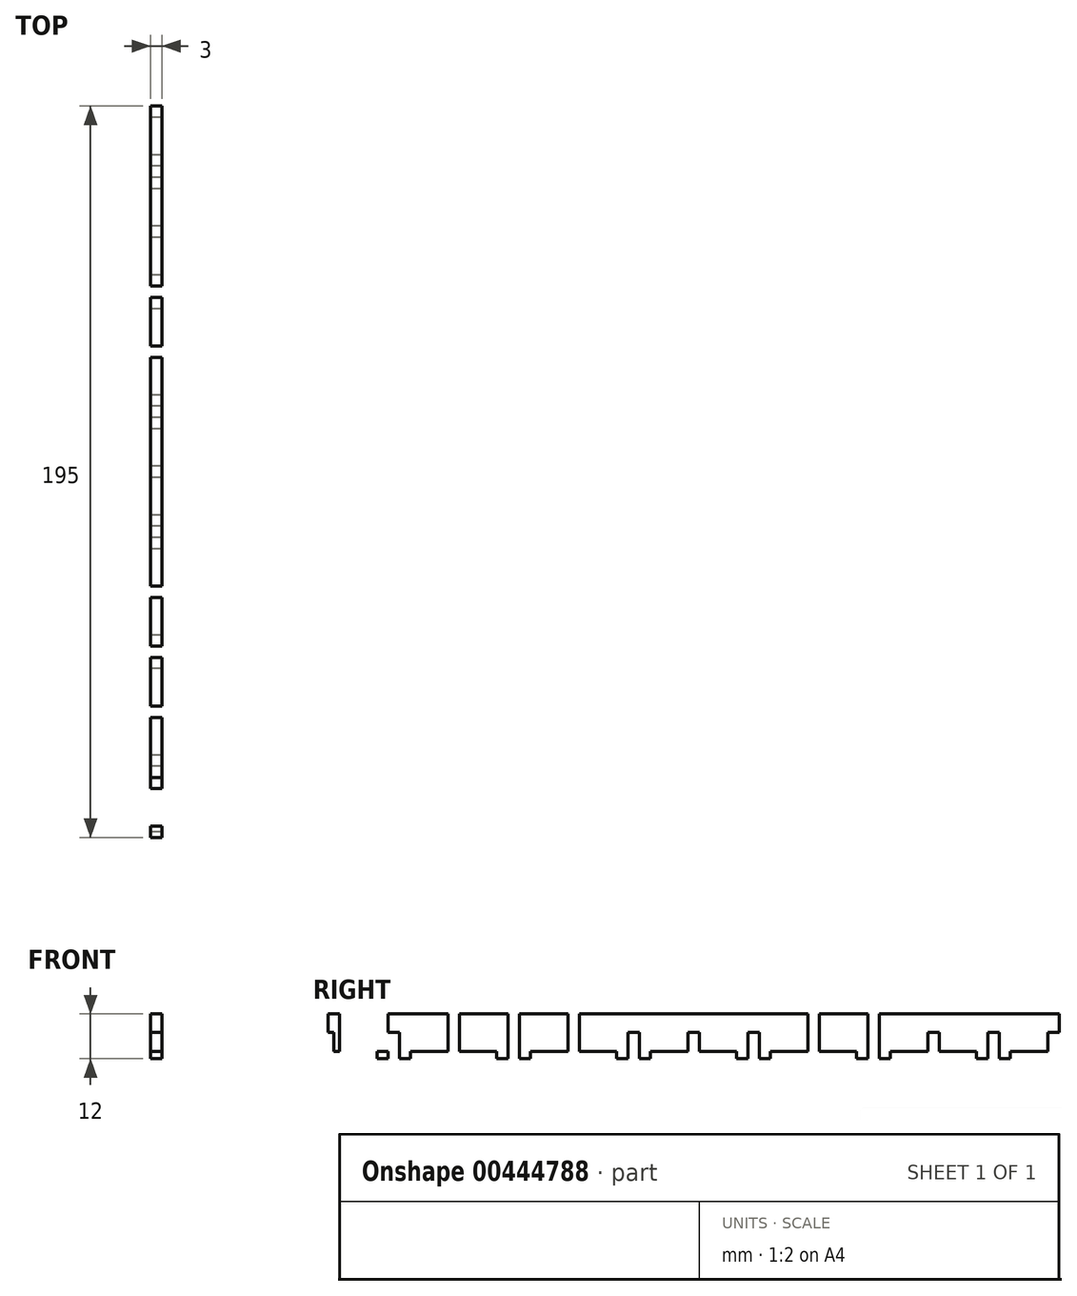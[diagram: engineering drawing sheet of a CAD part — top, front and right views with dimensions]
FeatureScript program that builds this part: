
annotation { "Feature Type Name" : "Feature", "Feature Type Description" : "" }
export const myFeature = defineFeature(function(context is Context, id is Id, definition is map)
    precondition{}
    {
        {
            var Q0;
            Q0=qCreatedBy(makeId("Right.planeOp"),FACE);
            var sketch = newSketch(context, id + "F0", { "sketchPlane" : qUnion([Q0])});
            skLineSegment(sketch, "E0", {"start": v(0, 0) * mm, "end": v(11.5, 0) * mm});
            skLineSegment(sketch, "E1", {"start": v(11.5, 0) * mm, "end": v(11.5, -2) * mm});
            skLineSegment(sketch, "E2", {"start": v(11.5, -2) * mm, "end": v(20.5, -2) * mm});
            skLineSegment(sketch, "E3", {"start": v(20.5, -2) * mm, "end": v(20.5, 0) * mm});
            skLineSegment(sketch, "E4", {"start": v(20.5, 0) * mm, "end": v(43.5, 0) * mm});
            skLineSegment(sketch, "E5", {"start": v(43.5, 0) * mm, "end": v(43.5, -2) * mm});
            skLineSegment(sketch, "E6", {"start": v(43.5, -2) * mm, "end": v(52.5, -2) * mm});
            skLineSegment(sketch, "E7", {"start": v(52.5, -2) * mm, "end": v(52.5, 0) * mm});
            skLineSegment(sketch, "E8", {"start": v(0, 0) * mm, "end": v(0, 10) * mm});
            skPoint(sketch, "E9.oppositeSnap0", {"position": v(0, 5) * mm});
            skLineSegment(sketch, "E9.bottom", {"start": v(0, 10) * mm, "end": v(-1.5, 10) * mm});
            skLineSegment(sketch, "E9.top", {"start": v(0, 5) * mm, "end": v(-1.5, 5) * mm});
            skLineSegment(sketch, "E9.left", {"start": v(0, 10) * mm, "end": v(0, 5) * mm});
            skLineSegment(sketch, "E9.right", {"start": v(-1.5, 10) * mm, "end": v(-1.5, 5) * mm});
            skLineSegment(sketch, "E10.bottom", {"start": v(14.5, 10) * mm, "end": v(17.5, 10) * mm});
            skLineSegment(sketch, "E10.top", {"start": v(14.5, 5) * mm, "end": v(17.5, 5) * mm});
            skLineSegment(sketch, "E10.left", {"start": v(14.5, 10) * mm, "end": v(14.5, 5) * mm});
            skLineSegment(sketch, "E10.right", {"start": v(17.5, 10) * mm, "end": v(17.5, 5) * mm});
            skLineSegment(sketch, "E11.top", {"start": v(0, 0) * mm, "end": v(-1.5, 0) * mm});
            skLineSegment(sketch, "E11.left", {"start": v(0, 5) * mm, "end": v(0, 0) * mm});
            skLineSegment(sketch, "E11.right", {"start": v(-1.5, 5) * mm, "end": v(-1.5, 0) * mm});
            skLineSegment(sketch, "E12.top", {"start": v(14.5, -2) * mm, "end": v(17.5, -2) * mm});
            skLineSegment(sketch, "E12.left", {"start": v(14.5, 5) * mm, "end": v(14.5, -2) * mm});
            skLineSegment(sketch, "E12.right", {"start": v(17.5, 5) * mm, "end": v(17.5, -2) * mm});
            skLineSegment(sketch, "E13.bottom", {"start": v(0, 10) * mm, "end": v(1.5, 10) * mm});
            skLineSegment(sketch, "E13.top", {"start": v(0, 5) * mm, "end": v(1.5, 5) * mm});
            skLineSegment(sketch, "E13.right", {"start": v(1.5, 10) * mm, "end": v(1.5, 5) * mm});
            skLineSegment(sketch, "E14.top", {"start": v(0, 0) * mm, "end": v(1.5, 0) * mm});
            skLineSegment(sketch, "E14.right", {"start": v(1.5, 5) * mm, "end": v(1.5, 0) * mm});
            skLineSegment(sketch, "E15.bottom", {"start": v(11.5, 10) * mm, "end": v(20.5, 10) * mm});
            skLineSegment(sketch, "E15.top", {"start": v(11.5, 13) * mm, "end": v(20.5, 13) * mm});
            skLineSegment(sketch, "E15.left", {"start": v(11.5, 10) * mm, "end": v(11.5, 13) * mm});
            skLineSegment(sketch, "E15.right", {"start": v(20.5, 10) * mm, "end": v(20.5, 13) * mm});
            skLineSegment(sketch, "E16", {"start": v(52.5, 0) * mm, "end": v(75.5, 0) * mm});
            skLineSegment(sketch, "E17", {"start": v(75.5, 0) * mm, "end": v(75.5, -2) * mm});
            skLineSegment(sketch, "E18", {"start": v(75.5, -2) * mm, "end": v(84.5, -2) * mm});
            skLineSegment(sketch, "E19", {"start": v(84.5, -2) * mm, "end": v(84.5, 0) * mm});
            skLineSegment(sketch, "E20", {"start": v(84.5, 0) * mm, "end": v(96, 0) * mm});
            skLineSegment(sketch, "E21", {"start": v(96, 0) * mm, "end": v(96, 19.13) * mm, "construction": true});
            skLineSegment(sketch, "E22", {"start": v(16, 10) * mm, "end": v(16, 11.65) * mm, "construction": true});
            skLineSegment(sketch, "E23.bottom", {"start": v(30.5, 0) * mm, "end": v(33.5, 0) * mm});
            skLineSegment(sketch, "E23.top", {"start": v(30.5, 5) * mm, "end": v(33.5, 5) * mm});
            skLineSegment(sketch, "E23.left", {"start": v(30.5, 0) * mm, "end": v(30.5, 5) * mm});
            skLineSegment(sketch, "E23.right", {"start": v(33.5, 0) * mm, "end": v(33.5, 5) * mm});
            skLineSegment(sketch, "E24.bottom", {"start": v(33.5, 5) * mm, "end": v(30.5, 5) * mm});
            skLineSegment(sketch, "E24.top", {"start": v(33.5, 10) * mm, "end": v(30.5, 10) * mm});
            skLineSegment(sketch, "E24.left", {"start": v(33.5, 5) * mm, "end": v(33.5, 10) * mm});
            skLineSegment(sketch, "E24.right", {"start": v(30.5, 5) * mm, "end": v(30.5, 10) * mm});
            skLineSegment(sketch, "E25", {"start": v(32, 0) * mm, "end": v(32, 2.31) * mm, "construction": true});
            skLineSegment(sketch, "E26.bottom", {"start": v(46.5, -2) * mm, "end": v(49.5, -2) * mm});
            skLineSegment(sketch, "E26.top", {"start": v(46.5, 5) * mm, "end": v(49.5, 5) * mm});
            skLineSegment(sketch, "E26.left", {"start": v(46.5, -2) * mm, "end": v(46.5, 5) * mm});
            skLineSegment(sketch, "E26.right", {"start": v(49.5, -2) * mm, "end": v(49.5, 5) * mm});
            skLineSegment(sketch, "E27.bottom", {"start": v(49.5, 5) * mm, "end": v(46.5, 5) * mm});
            skLineSegment(sketch, "E27.top", {"start": v(49.5, 10) * mm, "end": v(46.5, 10) * mm});
            skLineSegment(sketch, "E27.left", {"start": v(49.5, 5) * mm, "end": v(49.5, 10) * mm});
            skLineSegment(sketch, "E27.right", {"start": v(46.5, 5) * mm, "end": v(46.5, 10) * mm});
            skLineSegment(sketch, "E28.bottom", {"start": v(62.5, 0) * mm, "end": v(65.5, 0) * mm});
            skLineSegment(sketch, "E28.top", {"start": v(62.5, 5) * mm, "end": v(65.5, 5) * mm});
            skLineSegment(sketch, "E28.left", {"start": v(62.5, 0) * mm, "end": v(62.5, 5) * mm});
            skLineSegment(sketch, "E28.right", {"start": v(65.5, 0) * mm, "end": v(65.5, 5) * mm});
            skLineSegment(sketch, "E29.bottom", {"start": v(65.5, 5) * mm, "end": v(62.5, 5) * mm});
            skLineSegment(sketch, "E29.top", {"start": v(65.5, 10) * mm, "end": v(62.5, 10) * mm});
            skLineSegment(sketch, "E29.left", {"start": v(65.5, 5) * mm, "end": v(65.5, 10) * mm});
            skLineSegment(sketch, "E29.right", {"start": v(62.5, 5) * mm, "end": v(62.5, 10) * mm});
            skLineSegment(sketch, "E30.bottom", {"start": v(81.5, -2) * mm, "end": v(78.5, -2) * mm});
            skLineSegment(sketch, "E30.top", {"start": v(81.5, 5) * mm, "end": v(78.5, 5) * mm});
            skLineSegment(sketch, "E30.left", {"start": v(81.5, -2) * mm, "end": v(81.5, 5) * mm});
            skLineSegment(sketch, "E30.right", {"start": v(78.5, -2) * mm, "end": v(78.5, 5) * mm});
            skLineSegment(sketch, "E31.top", {"start": v(81.5, 10) * mm, "end": v(78.5, 10) * mm});
            skLineSegment(sketch, "E31.left", {"start": v(81.5, 5) * mm, "end": v(81.5, 10) * mm});
            skLineSegment(sketch, "E31.right", {"start": v(78.5, 5) * mm, "end": v(78.5, 10) * mm});
            skLineSegment(sketch, "E32.bottom", {"start": v(96, 0) * mm, "end": v(94.5, 0) * mm});
            skLineSegment(sketch, "E32.top", {"start": v(96, 5) * mm, "end": v(94.5, 5) * mm});
            skLineSegment(sketch, "E32.left", {"start": v(96, 0) * mm, "end": v(96, 5) * mm});
            skLineSegment(sketch, "E32.right", {"start": v(94.5, 0) * mm, "end": v(94.5, 5) * mm});
            skLineSegment(sketch, "E33.left", {"start": v(96, 5) * mm, "end": v(96, 5) * mm});
            skLineSegment(sketch, "E33.right", {"start": v(94.5, 5) * mm, "end": v(94.5, 5) * mm});
            skLineSegment(sketch, "E34.top", {"start": v(96, 10) * mm, "end": v(94.5, 10) * mm});
            skLineSegment(sketch, "E34.left", {"start": v(96, 5) * mm, "end": v(96, 10) * mm});
            skLineSegment(sketch, "E34.right", {"start": v(94.5, 5) * mm, "end": v(94.5, 10) * mm});
            skLineSegment(sketch, "E35", {"start": v(48, -2) * mm, "end": v(48, 0) * mm, "construction": true});
            skLineSegment(sketch, "E36", {"start": v(64, 0) * mm, "end": v(64, 2.67) * mm, "construction": true});
            skLineSegment(sketch, "E37", {"start": v(80, -2) * mm, "end": v(80, 0) * mm, "construction": true});
            skLineSegment(sketch, "E38", {"start": v(1.5, 10) * mm, "end": v(96, 10) * mm});
            skLineSegment(sketch, "E39.MirrorCS", {"start": v(96, 5) * mm, "end": v(97.5, 5) * mm});
            skLineSegment(sketch, "E40.MirrorCS", {"start": v(145.5, 5) * mm, "end": v(142.5, 5) * mm});
            skLineSegment(sketch, "E41.MirrorCS", {"start": v(110.5, 5) * mm, "end": v(113.5, 5) * mm});
            skLineSegment(sketch, "E42.MirrorCS", {"start": v(129.5, 5) * mm, "end": v(126.5, 5) * mm});
            skLineSegment(sketch, "E43.MirrorCS", {"start": v(177.5, 5) * mm, "end": v(174.5, 5) * mm});
            skLineSegment(sketch, "E44.MirrorCS", {"start": v(192, 5) * mm, "end": v(190.5, 5) * mm});
            skLineSegment(sketch, "E45.MirrorCS", {"start": v(192, 5) * mm, "end": v(193.5, 5) * mm});
            skLineSegment(sketch, "E46.MirrorCS", {"start": v(142.5, 5) * mm, "end": v(145.5, 5) * mm});
            skLineSegment(sketch, "E47.MirrorCS", {"start": v(126.5, 5) * mm, "end": v(129.5, 5) * mm});
            skLineSegment(sketch, "E48.MirrorCS", {"start": v(192, 10) * mm, "end": v(190.5, 10) * mm});
            skLineSegment(sketch, "E49.MirrorCS", {"start": v(171.5, -2) * mm, "end": v(171.5, 0) * mm});
            skLineSegment(sketch, "E50.MirrorCS", {"start": v(180.5, 0) * mm, "end": v(180.5, -2) * mm});
            skLineSegment(sketch, "E51.MirrorCS", {"start": v(177.5, 10) * mm, "end": v(174.5, 10) * mm});
            skLineSegment(sketch, "E52.MirrorCS", {"start": v(116.5, 0) * mm, "end": v(116.5, -2) * mm});
            skLineSegment(sketch, "E53.MirrorCS", {"start": v(177.5, -2) * mm, "end": v(174.5, -2) * mm});
            skLineSegment(sketch, "E54.MirrorCS", {"start": v(192, 0) * mm, "end": v(190.5, 0) * mm});
            skLineSegment(sketch, "E55.MirrorCS", {"start": v(126.5, 10) * mm, "end": v(129.5, 10) * mm});
            skLineSegment(sketch, "E56.MirrorCS", {"start": v(145.5, -2) * mm, "end": v(142.5, -2) * mm});
            skLineSegment(sketch, "E57.MirrorCS", {"start": v(110.5, -2) * mm, "end": v(113.5, -2) * mm});
            skLineSegment(sketch, "E58.MirrorCS", {"start": v(192, 0) * mm, "end": v(193.5, 0) * mm});
            skLineSegment(sketch, "E59.MirrorCS", {"start": v(96, 10) * mm, "end": v(97.5, 10) * mm});
            skLineSegment(sketch, "E60.MirrorCS", {"start": v(110.5, 10) * mm, "end": v(113.5, 10) * mm});
            skLineSegment(sketch, "E61.MirrorCS", {"start": v(142.5, 10) * mm, "end": v(145.5, 10) * mm});
            skLineSegment(sketch, "E62.MirrorCS", {"start": v(107.5, -2) * mm, "end": v(107.5, 0) * mm});
            skLineSegment(sketch, "E63.MirrorCS", {"start": v(192, 10) * mm, "end": v(193.5, 10) * mm});
            skLineSegment(sketch, "E64.MirrorCS", {"start": v(96, 0) * mm, "end": v(97.5, 0) * mm});
            skLineSegment(sketch, "E65.MirrorCS", {"start": v(139.5, -2) * mm, "end": v(139.5, 0) * mm});
            skLineSegment(sketch, "E66.MirrorCS", {"start": v(129.5, 0) * mm, "end": v(126.5, 0) * mm});
            skLineSegment(sketch, "E67.MirrorCS", {"start": v(148.5, 0) * mm, "end": v(148.5, -2) * mm});
            skLineSegment(sketch, "E68.MirrorCS", {"start": v(192, 5) * mm, "end": v(192, 0) * mm});
            skLineSegment(sketch, "E69.MirrorCS", {"start": v(112, -2) * mm, "end": v(112, 0) * mm, "construction": true});
            skLineSegment(sketch, "E70.MirrorCS", {"start": v(176, 10) * mm, "end": v(176, 11.65) * mm, "construction": true});
            skLineSegment(sketch, "E71.MirrorCS", {"start": v(192, 10) * mm, "end": v(192, 5) * mm});
            skLineSegment(sketch, "E72.MirrorCS", {"start": v(161.5, 0) * mm, "end": v(158.5, 0) * mm});
            skLineSegment(sketch, "E73.MirrorCS", {"start": v(128, 0) * mm, "end": v(128, 2.67) * mm, "construction": true});
            skLineSegment(sketch, "E74.MirrorCS", {"start": v(160, 0) * mm, "end": v(160, 2.31) * mm, "construction": true});
            skLineSegment(sketch, "E75.MirrorCS", {"start": v(144, -2) * mm, "end": v(144, 0) * mm, "construction": true});
            skLineSegment(sketch, "E76.MirrorCS", {"start": v(161.5, 5) * mm, "end": v(158.5, 5) * mm});
            skLineSegment(sketch, "E77.MirrorCS", {"start": v(171.5, 0) * mm, "end": v(148.5, 0) * mm});
            skLineSegment(sketch, "E78.MirrorCS", {"start": v(180.5, -2) * mm, "end": v(171.5, -2) * mm});
            skLineSegment(sketch, "E79.MirrorCS", {"start": v(192, 0) * mm, "end": v(180.5, 0) * mm});
            skLineSegment(sketch, "E80.MirrorCS", {"start": v(177.5, 10) * mm, "end": v(177.5, 5) * mm});
            skLineSegment(sketch, "E81.MirrorCS", {"start": v(158.5, 0) * mm, "end": v(158.5, 5) * mm});
            skLineSegment(sketch, "E82.MirrorCS", {"start": v(129.5, 0) * mm, "end": v(129.5, 5) * mm});
            skLineSegment(sketch, "E83.MirrorCS", {"start": v(97.5, 5) * mm, "end": v(97.5, 10) * mm});
            skPoint(sketch, "E84.MirrorP", {"position": v(192, 5) * mm});
            skLineSegment(sketch, "E85.MirrorCS", {"start": v(139.5, 0) * mm, "end": v(116.5, 0) * mm});
            skLineSegment(sketch, "E86.MirrorCS", {"start": v(126.5, 5) * mm, "end": v(126.5, 10) * mm});
            skLineSegment(sketch, "E87.MirrorCS", {"start": v(161.5, 5) * mm, "end": v(161.5, 10) * mm});
            skLineSegment(sketch, "E88.MirrorCS", {"start": v(180.5, 10) * mm, "end": v(180.5, 13) * mm});
            skLineSegment(sketch, "E89.MirrorCS", {"start": v(180.5, 13) * mm, "end": v(171.5, 13) * mm});
            skLineSegment(sketch, "E90.MirrorCS", {"start": v(158.5, 5) * mm, "end": v(158.5, 10) * mm});
            skLineSegment(sketch, "E91.MirrorCS", {"start": v(161.5, 0) * mm, "end": v(161.5, 5) * mm});
            skLineSegment(sketch, "E92.MirrorCS", {"start": v(107.5, 0) * mm, "end": v(96, 0) * mm});
            skLineSegment(sketch, "E93.MirrorCS", {"start": v(142.5, 5) * mm, "end": v(142.5, 10) * mm});
            skLineSegment(sketch, "E94.MirrorCS", {"start": v(193.5, 5) * mm, "end": v(193.5, 0) * mm});
            skLineSegment(sketch, "E95.MirrorCS", {"start": v(110.5, 5) * mm, "end": v(110.5, 10) * mm});
            skLineSegment(sketch, "E96.MirrorCS", {"start": v(180.5, 10) * mm, "end": v(171.5, 10) * mm});
            skLineSegment(sketch, "E97.MirrorCS", {"start": v(158.5, 10) * mm, "end": v(161.5, 10) * mm});
            skLineSegment(sketch, "E98.MirrorCS", {"start": v(145.5, 5) * mm, "end": v(145.5, 10) * mm});
            skLineSegment(sketch, "E99.MirrorCS", {"start": v(113.5, -2) * mm, "end": v(113.5, 5) * mm});
            skLineSegment(sketch, "E100.MirrorCS", {"start": v(174.5, 5) * mm, "end": v(174.5, -2) * mm});
            skLineSegment(sketch, "E101.MirrorCS", {"start": v(142.5, -2) * mm, "end": v(142.5, 5) * mm});
            skLineSegment(sketch, "E102.MirrorCS", {"start": v(113.5, 5) * mm, "end": v(113.5, 10) * mm});
            skLineSegment(sketch, "E103.MirrorCS", {"start": v(190.5, 10) * mm, "end": v(96, 10) * mm});
            skLineSegment(sketch, "E104.MirrorCS", {"start": v(190.5, 5) * mm, "end": v(190.5, 0) * mm});
            skLineSegment(sketch, "E105.MirrorCS", {"start": v(158.5, 5) * mm, "end": v(161.5, 5) * mm});
            skLineSegment(sketch, "E106.MirrorCS", {"start": v(126.5, 0) * mm, "end": v(126.5, 5) * mm});
            skLineSegment(sketch, "E107.MirrorCS", {"start": v(97.5, 0) * mm, "end": v(97.5, 5) * mm});
            skLineSegment(sketch, "E108.MirrorCS", {"start": v(174.5, 10) * mm, "end": v(174.5, 5) * mm});
            skLineSegment(sketch, "E109.MirrorCS", {"start": v(110.5, -2) * mm, "end": v(110.5, 5) * mm});
            skLineSegment(sketch, "E110.MirrorCS", {"start": v(177.5, 5) * mm, "end": v(177.5, -2) * mm});
            skLineSegment(sketch, "E111.MirrorCS", {"start": v(116.5, -2) * mm, "end": v(107.5, -2) * mm});
            skLineSegment(sketch, "E112.MirrorCS", {"start": v(145.5, -2) * mm, "end": v(145.5, 5) * mm});
            skLineSegment(sketch, "E113.MirrorCS", {"start": v(193.5, 10) * mm, "end": v(193.5, 5) * mm});
            skLineSegment(sketch, "E114.MirrorCS", {"start": v(129.5, 5) * mm, "end": v(129.5, 10) * mm});
            skLineSegment(sketch, "E115.MirrorCS", {"start": v(192, 0) * mm, "end": v(192, 10) * mm});
            skLineSegment(sketch, "E116.MirrorCS", {"start": v(148.5, -2) * mm, "end": v(139.5, -2) * mm});
            skLineSegment(sketch, "E117.MirrorCS", {"start": v(171.5, 10) * mm, "end": v(171.5, 13) * mm});
            skLineSegment(sketch, "E118.MirrorCS", {"start": v(190.5, 10) * mm, "end": v(190.5, 5) * mm});
            skLineSegment(sketch, "E119.top", {"start": v(14.5, 13) * mm, "end": v(17.5, 13) * mm});
            skLineSegment(sketch, "E119.left", {"start": v(14.5, 10) * mm, "end": v(14.5, 13) * mm});
            skLineSegment(sketch, "E119.right", {"start": v(17.5, 10) * mm, "end": v(17.5, 13) * mm});
            skLineSegment(sketch, "E120.bottom", {"start": v(174.5, 10) * mm, "end": v(177.5, 10) * mm});
            skLineSegment(sketch, "E120.top", {"start": v(174.5, 13) * mm, "end": v(177.5, 13) * mm});
            skLineSegment(sketch, "E120.left", {"start": v(174.5, 10) * mm, "end": v(174.5, 13) * mm});
            skLineSegment(sketch, "E120.right", {"start": v(177.5, 10) * mm, "end": v(177.5, 13) * mm});
            skLineSegment(sketch, "E121", {"start": v(11.5, 0) * mm, "end": v(180.5, 0) * mm});
            skSolve(sketch);
        }
        {
            var Q0;
            {var subQ5=sQuery(id+"F0.wireOp",EDGE,"E0");Q0=makeQuery(id+"F0.imprint","IMPRINT",FACE,{"disambiguationData":[TD([[makeQuery(id+"F0.imprint","IMPRINT",EDGE,{"derivedFrom":subQ5}),1.0]])]});}
            var Q1;
            {var subQ2=sQuery(id+"F0.wireOp",EDGE,"E10.right");Q1=makeQuery(id+"F0.imprint","IMPRINT",FACE,{"disambiguationData":[TD([[makeQuery(id+"F0.imprint","IMPRINT",EDGE,{"derivedFrom":subQ2}),1.0]])]});}
            var Q2;
            {var subQ0=sQuery(id+"F0.wireOp",EDGE,"E5");Q2=makeQuery(id+"F0.imprint","IMPRINT",FACE,{"disambiguationData":[TD([[makeQuery(id+"F0.imprint","IMPRINT",EDGE,{"derivedFrom":subQ0}),1.0]])]});}
            var Q3;
            Q3=makeQuery(id+"F0.imprint","IMPRINT",FACE,{"disambiguationData":[TD([[makeQuery(id+"F0.imprint","IMPRINT",EDGE,{"derivedFrom":sQuery(id+"F0.wireOp",EDGE,"E13.bottom")}),-1.0]])]});
            var Q4;
            Q4=makeQuery(id+"F0.imprint","IMPRINT",FACE,{"disambiguationData":[TD([[makeQuery(id+"F0.imprint","IMPRINT",EDGE,{"derivedFrom":sQuery(id+"F0.wireOp",EDGE,"E9.bottom")}),1.0]])]});
            var Q5;
            Q5=makeQuery(id+"F0.imprint","IMPRINT",FACE,{"disambiguationData":[TD([[makeQuery(id+"F0.imprint","IMPRINT",EDGE,{"derivedFrom":sQuery(id+"F0.wireOp",EDGE,"E10.left")}),1.0]])]});
            var Q6;
            Q6=makeQuery(id+"F0.imprint","IMPRINT",FACE,{"disambiguationData":[TD([[makeQuery(id+"F0.imprint","IMPRINT",EDGE,{"derivedFrom":sQuery(id+"F0.wireOp",EDGE,"E24.bottom")}),-1.0]])]});
            var Q7;
            Q7=makeQuery(id+"F0.imprint","IMPRINT",FACE,{"disambiguationData":[TD([[makeQuery(id+"F0.imprint","IMPRINT",EDGE,{"derivedFrom":sQuery(id+"F0.wireOp",EDGE,"E27.bottom")}),-1.0]])]});
            var Q8;
            {var subQ0=sQuery(id+"F0.wireOp",EDGE,"E7");Q8=makeQuery(id+"F0.imprint","IMPRINT",FACE,{"disambiguationData":[TD([[makeQuery(id+"F0.imprint","IMPRINT",EDGE,{"derivedFrom":subQ0}),1.0]])]});}
            var Q9;
            Q9=makeQuery(id+"F0.imprint","IMPRINT",FACE,{"disambiguationData":[TD([[makeQuery(id+"F0.imprint","IMPRINT",EDGE,{"derivedFrom":sQuery(id+"F0.wireOp",EDGE,"E29.bottom")}),-1.0]])]});
            var Q10;
            {var subQ0=sQuery(id+"F0.wireOp",EDGE,"E17");Q10=makeQuery(id+"F0.imprint","IMPRINT",FACE,{"disambiguationData":[TD([[makeQuery(id+"F0.imprint","IMPRINT",EDGE,{"derivedFrom":subQ0}),1.0]])]});}
            var Q11;
            Q11=makeQuery(id+"F0.imprint","IMPRINT",FACE,{"disambiguationData":[TD([[makeQuery(id+"F0.imprint","IMPRINT",EDGE,{"derivedFrom":sQuery(id+"F0.wireOp",EDGE,"E30.top")}),-1.0]])]});
            var Q12;
            {var subQ0=sQuery(id+"F0.wireOp",EDGE,"E19");Q12=makeQuery(id+"F0.imprint","IMPRINT",FACE,{"disambiguationData":[TD([[makeQuery(id+"F0.imprint","IMPRINT",EDGE,{"derivedFrom":subQ0}),1.0]])]});}
            var Q13;
            Q13=makeQuery(id+"F0.imprint","IMPRINT",FACE,{"disambiguationData":[TD([[makeQuery(id+"F0.imprint","IMPRINT",EDGE,{"derivedFrom":sQuery(id+"F0.wireOp",EDGE,"E32.top")}),-1.0]])]});
            var Q14;
            Q14=makeQuery(id+"F0.imprint","IMPRINT",FACE,{"disambiguationData":[TD([[makeQuery(id+"F0.imprint","IMPRINT",EDGE,{"derivedFrom":sQuery(id+"F0.wireOp",EDGE,"E39.MirrorCS")}),1.0]])]});
            var Q15;
            {var subQ0=sQuery(id+"F0.wireOp",EDGE,"E62.MirrorCS");Q15=makeQuery(id+"F0.imprint","IMPRINT",FACE,{"disambiguationData":[TD([[makeQuery(id+"F0.imprint","IMPRINT",EDGE,{"derivedFrom":subQ0}),-1.0]])]});}
            var Q16;
            Q16=makeQuery(id+"F0.imprint","IMPRINT",FACE,{"disambiguationData":[TD([[makeQuery(id+"F0.imprint","IMPRINT",EDGE,{"derivedFrom":sQuery(id+"F0.wireOp",EDGE,"E41.MirrorCS")}),1.0]])]});
            var Q17;
            {var subQ0=sQuery(id+"F0.wireOp",EDGE,"E52.MirrorCS");Q17=makeQuery(id+"F0.imprint","IMPRINT",FACE,{"disambiguationData":[TD([[makeQuery(id+"F0.imprint","IMPRINT",EDGE,{"derivedFrom":subQ0}),-1.0]])]});}
            var Q18;
            Q18=makeQuery(id+"F0.imprint","IMPRINT",FACE,{"disambiguationData":[TD([[makeQuery(id+"F0.imprint","IMPRINT",EDGE,{"derivedFrom":sQuery(id+"F0.wireOp",EDGE,"E47.MirrorCS")}),1.0]])]});
            var Q19;
            {var subQ0=sQuery(id+"F0.wireOp",EDGE,"E65.MirrorCS");Q19=makeQuery(id+"F0.imprint","IMPRINT",FACE,{"disambiguationData":[TD([[makeQuery(id+"F0.imprint","IMPRINT",EDGE,{"derivedFrom":subQ0}),-1.0]])]});}
            var Q20;
            Q20=makeQuery(id+"F0.imprint","IMPRINT",FACE,{"disambiguationData":[TD([[makeQuery(id+"F0.imprint","IMPRINT",EDGE,{"derivedFrom":sQuery(id+"F0.wireOp",EDGE,"E46.MirrorCS")}),1.0]])]});
            var Q21;
            {var subQ0=sQuery(id+"F0.wireOp",EDGE,"E67.MirrorCS");Q21=makeQuery(id+"F0.imprint","IMPRINT",FACE,{"disambiguationData":[TD([[makeQuery(id+"F0.imprint","IMPRINT",EDGE,{"derivedFrom":subQ0}),-1.0]])]});}
            var Q22;
            {var subQ0=sQuery(id+"F0.wireOp",EDGE,"E87.MirrorCS");Q22=makeQuery(id+"F0.imprint","IMPRINT",FACE,{"disambiguationData":[TD([[makeQuery(id+"F0.imprint","IMPRINT",EDGE,{"derivedFrom":subQ0}),1.0]])]});}
            var Q23;
            {var subQ0=sQuery(id+"F0.wireOp",EDGE,"E49.MirrorCS");Q23=makeQuery(id+"F0.imprint","IMPRINT",FACE,{"disambiguationData":[TD([[makeQuery(id+"F0.imprint","IMPRINT",EDGE,{"derivedFrom":subQ0}),-1.0]])]});}
            var Q24;
            Q24=makeQuery(id+"F0.imprint","IMPRINT",FACE,{"disambiguationData":[TD([[makeQuery(id+"F0.imprint","IMPRINT",EDGE,{"derivedFrom":sQuery(id+"F0.wireOp",EDGE,"E43.MirrorCS")}),-1.0]])]});
            var Q25;
            {var subQ0=sQuery(id+"F0.wireOp",EDGE,"E50.MirrorCS");Q25=makeQuery(id+"F0.imprint","IMPRINT",FACE,{"disambiguationData":[TD([[makeQuery(id+"F0.imprint","IMPRINT",EDGE,{"derivedFrom":subQ0}),-1.0]])]});}
            var Q26;
            {var subQ0=sQuery(id+"F0.wireOp",EDGE,"E44.MirrorCS");Q26=makeQuery(id+"F0.imprint","IMPRINT",FACE,{"disambiguationData":[TD([[makeQuery(id+"F0.imprint","IMPRINT",EDGE,{"derivedFrom":subQ0}),-1.0]])]});}
            var Q27;
            {var subQ0=sQuery(id+"F0.wireOp",EDGE,"E45.MirrorCS");Q27=makeQuery(id+"F0.imprint","IMPRINT",FACE,{"disambiguationData":[TD([[makeQuery(id+"F0.imprint","IMPRINT",EDGE,{"derivedFrom":subQ0}),1.0]])]});}
            var Q28;
            {var subQ0=sQuery(id+"F0.wireOp",EDGE,"E1");Q28=makeQuery(id+"F0.imprint","IMPRINT",FACE,{"disambiguationData":[TD([[makeQuery(id+"F0.imprint","IMPRINT",EDGE,{"derivedFrom":subQ0}),1.0]])]});}
            var Q29;
            {var subQ0=sQuery(id+"F0.wireOp",EDGE,"E3");Q29=makeQuery(id+"F0.imprint","IMPRINT",FACE,{"disambiguationData":[TD([[makeQuery(id+"F0.imprint","IMPRINT",EDGE,{"derivedFrom":subQ0}),1.0]])]});}
            var Q30;
            {var subQ1=sQuery(id+"F0.wireOp",EDGE,"E23.right");Q30=makeQuery(id+"F0.imprint","IMPRINT",FACE,{"disambiguationData":[TD([[makeQuery(id+"F0.imprint","IMPRINT",EDGE,{"derivedFrom":subQ1}),-1.0]])]});}
            var Q31;
            {var subQ2=sQuery(id+"F0.wireOp",EDGE,"E27.left");Q31=makeQuery(id+"F0.imprint","IMPRINT",FACE,{"disambiguationData":[TD([[makeQuery(id+"F0.imprint","IMPRINT",EDGE,{"derivedFrom":subQ2}),-1.0]])]});}
            var Q32;
            {var subQ1=sQuery(id+"F0.wireOp",EDGE,"E28.right");Q32=makeQuery(id+"F0.imprint","IMPRINT",FACE,{"disambiguationData":[TD([[makeQuery(id+"F0.imprint","IMPRINT",EDGE,{"derivedFrom":subQ1}),-1.0]])]});}
            var Q33;
            {var subQ2=sQuery(id+"F0.wireOp",EDGE,"E31.left");Q33=makeQuery(id+"F0.imprint","IMPRINT",FACE,{"disambiguationData":[TD([[makeQuery(id+"F0.imprint","IMPRINT",EDGE,{"derivedFrom":subQ2}),-1.0]])]});}
            var Q34;
            {var subQ2=sQuery(id+"F0.wireOp",EDGE,"E83.MirrorCS");Q34=makeQuery(id+"F0.imprint","IMPRINT",FACE,{"disambiguationData":[TD([[makeQuery(id+"F0.imprint","IMPRINT",EDGE,{"derivedFrom":subQ2}),-1.0]])]});}
            var Q35;
            {var subQ1=sQuery(id+"F0.wireOp",EDGE,"E86.MirrorCS");Q35=makeQuery(id+"F0.imprint","IMPRINT",FACE,{"disambiguationData":[TD([[makeQuery(id+"F0.imprint","IMPRINT",EDGE,{"derivedFrom":subQ1}),1.0]])]});}
            var Q36;
            {var subQ6=sQuery(id+"F0.wireOp",EDGE,"E82.MirrorCS");Q36=makeQuery(id+"F0.imprint","IMPRINT",FACE,{"disambiguationData":[TD([[makeQuery(id+"F0.imprint","IMPRINT",EDGE,{"derivedFrom":subQ6}),-1.0]])]});}
            var Q37;
            {var subQ7=sQuery(id+"F0.wireOp",EDGE,"E81.MirrorCS");Q37=makeQuery(id+"F0.imprint","IMPRINT",FACE,{"disambiguationData":[TD([[makeQuery(id+"F0.imprint","IMPRINT",EDGE,{"derivedFrom":subQ7}),1.0]])]});}
            var Q38;
            {var subQ7=sQuery(id+"F0.wireOp",EDGE,"E87.MirrorCS");Q38=makeQuery(id+"F0.imprint","IMPRINT",FACE,{"disambiguationData":[TD([[makeQuery(id+"F0.imprint","IMPRINT",EDGE,{"derivedFrom":subQ7}),-1.0]])]});}
            var Q39;
            {var subQ1=sQuery(id+"F0.wireOp",EDGE,"E80.MirrorCS");Q39=makeQuery(id+"F0.imprint","IMPRINT",FACE,{"disambiguationData":[TD([[makeQuery(id+"F0.imprint","IMPRINT",EDGE,{"derivedFrom":subQ1}),1.0]])]});}
            extrude(context, id + "F1", {"entities" : qUnion([Q0, Q1, Q2, Q3, Q4, Q5, Q6, Q7, Q8, Q9, Q10, Q11, Q12, Q13, Q14, Q15, Q16, Q17, Q18, Q19, Q20, Q21, Q22, Q23, Q24, Q25, Q26, Q27, Q28, Q29, Q30, Q31, Q32, Q33, Q34, Q35, Q36, Q37, Q38, Q39]), "depth" : 3 * mm});
        }
    });
